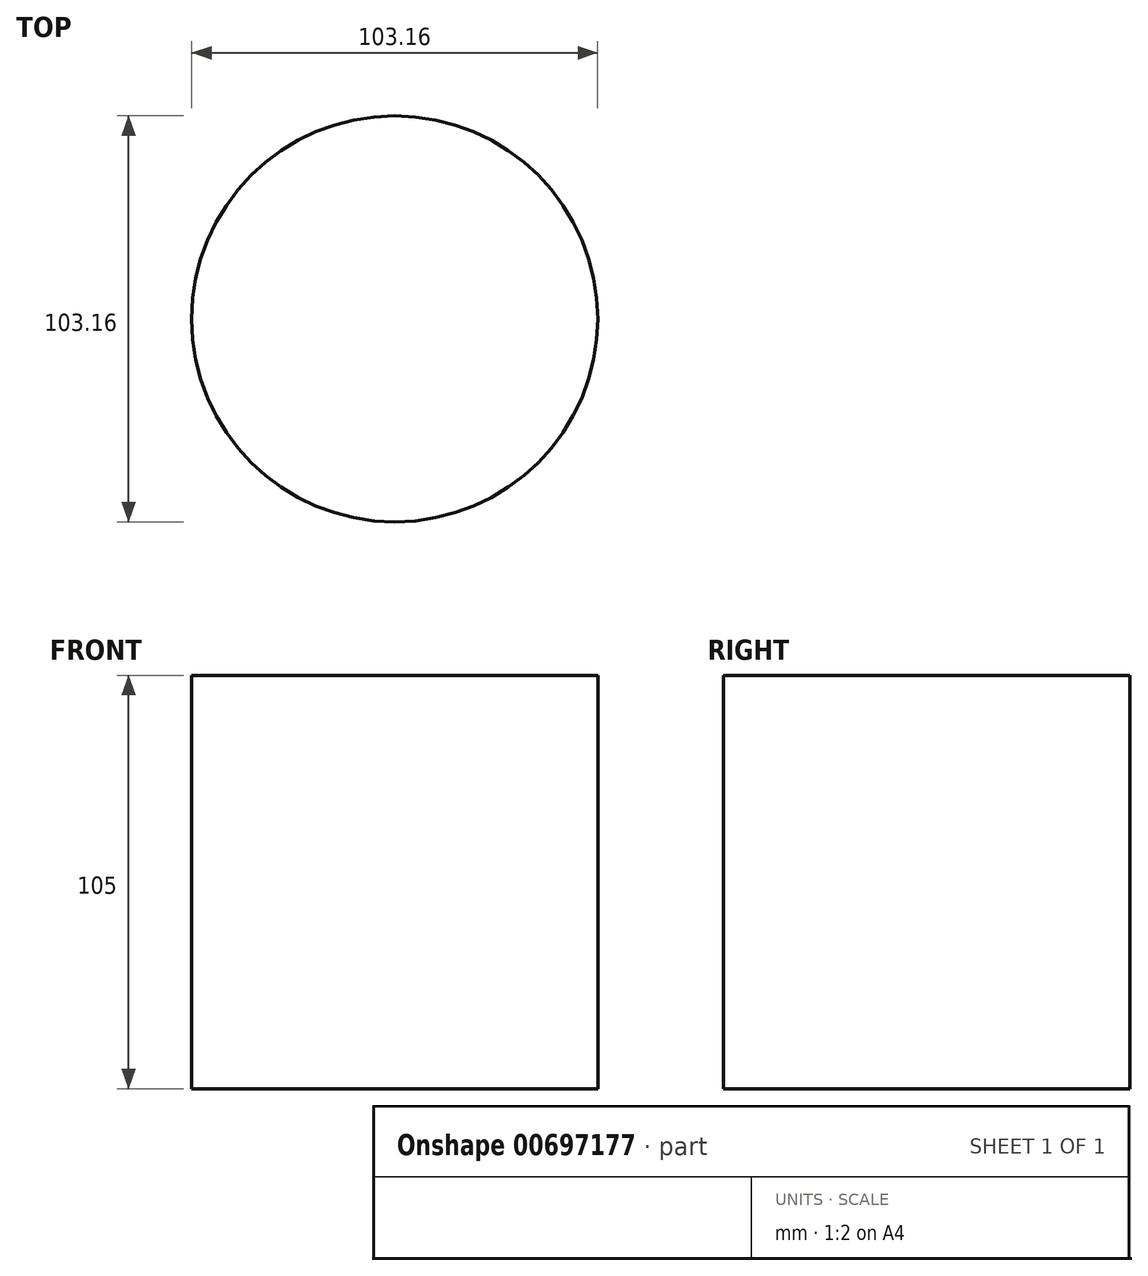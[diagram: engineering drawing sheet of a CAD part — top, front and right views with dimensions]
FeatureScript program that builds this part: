
annotation { "Feature Type Name" : "Feature", "Feature Type Description" : "" }
export const myFeature = defineFeature(function(context is Context, id is Id, definition is map)
    precondition{}
    {
        {
            var Q0;
            Q0=qCreatedBy(makeId("Top.planeOp"),FACE);
            var sketch = newSketch(context, id + "F0", { "sketchPlane" : qUnion([Q0])});
            skCircle(sketch, "E0", {"center": v(0, 0) * mm, "radius": 51.58 * mm});
            skSolve(sketch);
        }
        {
            var Q0;
            Q0 = qSketchRegion(id + "F0", true);
            extrude(context, id + "F1", {"entities" : qUnion([Q0]), "depth" : 105 * mm, "offsetDistance" : 25.4 * mm});
        }
        {
            var Q0;
            Q0=qCreatedBy(makeId("Right.planeOp"),FACE);
            cPlane(context, id + "F2", {"entities" : qUnion([Q0]), "cplaneType" : CPlaneType.OFFSET, "offset" : 50 * mm, "width" : 152.4 * mm, "height" : 152.4 * mm});
        }
    });
